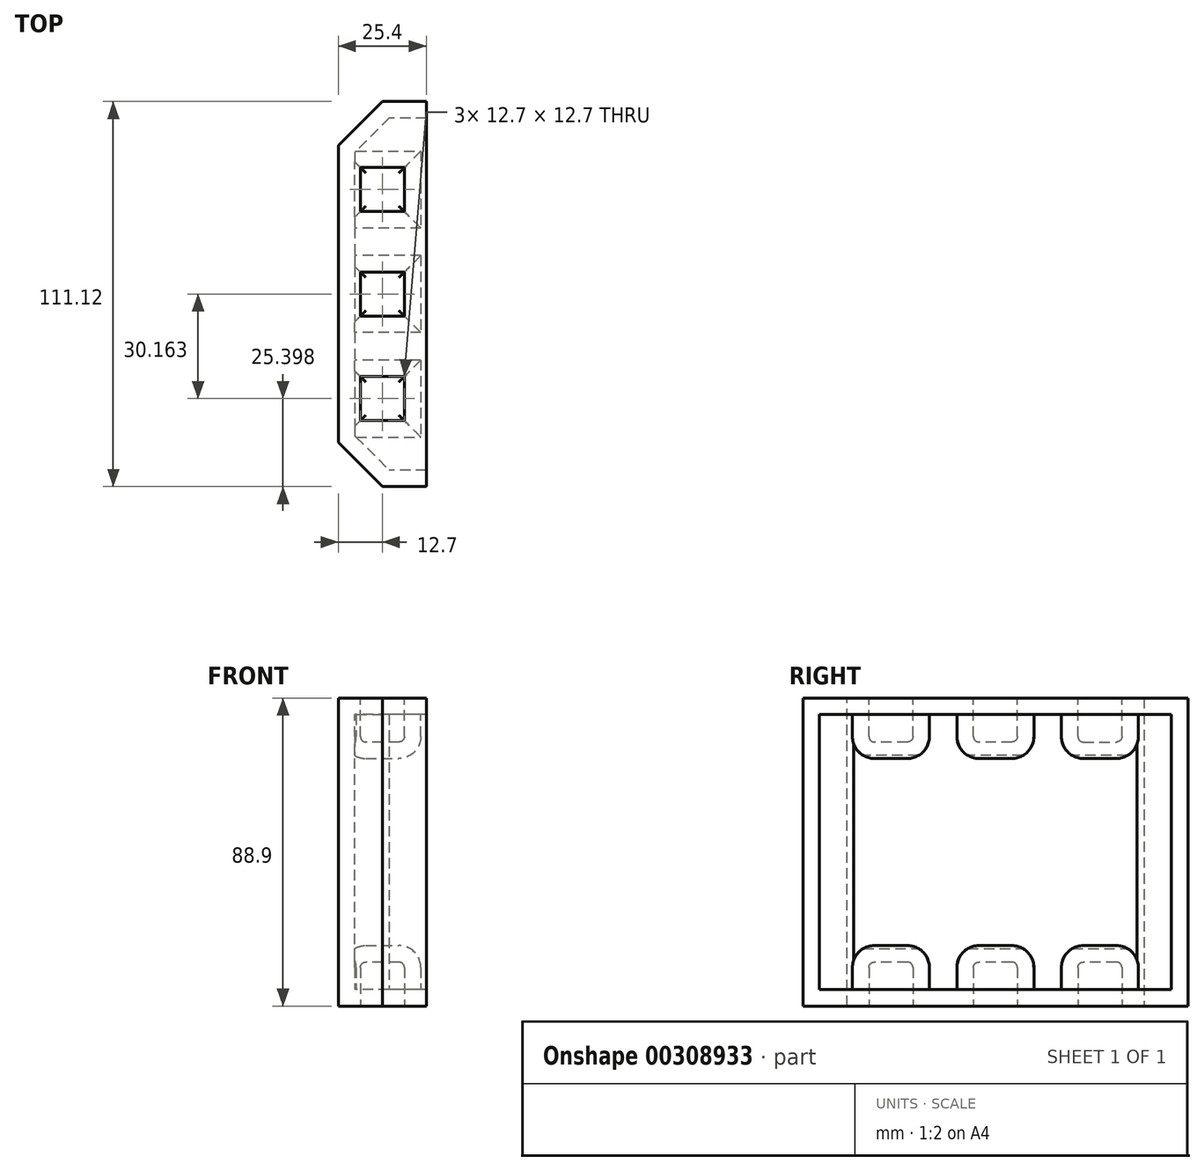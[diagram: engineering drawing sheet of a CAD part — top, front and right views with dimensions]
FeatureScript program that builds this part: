
annotation { "Feature Type Name" : "Feature", "Feature Type Description" : "" }
export const myFeature = defineFeature(function(context is Context, id is Id, definition is map)
    precondition{}
    {
        {
            var Q0;
            Q0=qCreatedBy(makeId("Right.planeOp"),FACE);
            var sketch = newSketch(context, id + "F0", { "sketchPlane" : qUnion([Q0])});
            skLineSegment(sketch, "E0.bottom", {"start": v(55.56, -44.45) * mm, "end": v(-55.56, -44.45) * mm});
            skLineSegment(sketch, "E0.top", {"start": v(55.56, 44.45) * mm, "end": v(-55.56, 44.45) * mm});
            skLineSegment(sketch, "E0.left", {"start": v(55.56, -44.45) * mm, "end": v(55.56, 44.45) * mm});
            skLineSegment(sketch, "E0.right", {"start": v(-55.56, -44.45) * mm, "end": v(-55.56, 44.45) * mm});
            skPoint(sketch, "E0.middle", {"position": v(0, 0) * mm});
            skSolve(sketch);
        }
        {
            var Q0;
            Q0=qSketchRegion(id+"F0",true);
            extrude(context, id + "F1", {"entities" : qUnion([Q0]), "depth" : 25.4 * mm});
        }
        {
            var Q0;
            Q0=makeQuery(id+"F1.opExtrude","CAP_EDGE",EDGE,{"disambiguationData":[OSD([sQuery(id+"F0.wireOp",EDGE,"E0.right")])],"isStart":true});
            var Q1;
            Q1=makeQuery(id+"F1.opExtrude","CAP_EDGE",EDGE,{"disambiguationData":[OSD([sQuery(id+"F0.wireOp",EDGE,"E0.left")])],"isStart":true});
            chamfer(context, id + "F2", {"entities" : qUnion([Q0, Q1]), "width" : 12.7 * mm, "tangentPropagation" : true});
        }
        {
            var Q0;
            Q0=makeQuery(id+"F1.opExtrude","SWEPT_FACE",FACE,{"disambiguationData":[OSD([sQuery(id+"F0.wireOp",EDGE,"E0.top")])]});
            var sketch = newSketch(context, id + "F3", { "sketchPlane" : qUnion([Q0])});
            skLineSegment(sketch, "E1.bottom", {"start": v(19.05, 23.81) * mm, "end": v(6.35, 23.81) * mm});
            skLineSegment(sketch, "E1.top", {"start": v(19.05, 36.51) * mm, "end": v(6.35, 36.51) * mm});
            skLineSegment(sketch, "E1.left", {"start": v(19.05, 23.81) * mm, "end": v(19.05, 36.51) * mm});
            skLineSegment(sketch, "E1.right", {"start": v(6.35, 23.81) * mm, "end": v(6.35, 36.51) * mm});
            skPoint(sketch, "E1.middle", {"position": v(12.7, 30.16) * mm});
            skPoint(sketch, "E1.cornerSnap0", {"position": v(19.05, 55.56) * mm});
            skLineSegment(sketch, "E2.bottom", {"start": v(19.05, -23.81) * mm, "end": v(6.35, -23.81) * mm});
            skLineSegment(sketch, "E2.top", {"start": v(19.05, -36.51) * mm, "end": v(6.35, -36.51) * mm});
            skLineSegment(sketch, "E2.left", {"start": v(19.05, -23.81) * mm, "end": v(19.05, -36.51) * mm});
            skLineSegment(sketch, "E2.right", {"start": v(6.35, -23.81) * mm, "end": v(6.35, -36.51) * mm});
            skPoint(sketch, "E2.middle", {"position": v(12.7, -30.16) * mm});
            skPoint(sketch, "E2.cornerSnap0", {"position": v(19.05, -55.56) * mm});
            skLineSegment(sketch, "E3.bottom", {"start": v(19.05, 6.35) * mm, "end": v(6.35, 6.35) * mm});
            skLineSegment(sketch, "E3.top", {"start": v(19.05, -6.35) * mm, "end": v(6.35, -6.35) * mm});
            skLineSegment(sketch, "E3.left", {"start": v(19.05, 6.35) * mm, "end": v(19.05, -6.35) * mm});
            skLineSegment(sketch, "E3.right", {"start": v(6.35, 6.35) * mm, "end": v(6.35, -6.35) * mm});
            skPoint(sketch, "E3.middle", {"position": v(12.7, 0) * mm});
            skSolve(sketch);
        }
        {
            var Q0;
            Q0=qSketchRegion(id+"F3",true);
            extrude(context, id + "F4", {"entities" : qUnion([Q0]), "operationType" : NewBodyOperationType.REMOVE, "oppositeDirection" : true, "depth" : 12.7 * mm});
        }
        {
            var Q0;
            Q0=makeQuery(id+"F4.boolean.opBoolean","COPY",FACE,{"derivedFrom":makeQuery(id+"F4.opExtrude","CAP_FACE",FACE,{"disambiguationData":[OSD([sQuery(id+"F3.wireOp",EDGE,"E1.bottom"),sQuery(id+"F3.wireOp",EDGE,"E1.top"),sQuery(id+"F3.wireOp",EDGE,"E1.left"),sQuery(id+"F3.wireOp",EDGE,"E1.right")])],"isStart":false})});
            var Q1;
            Q1=makeQuery(id+"F4.boolean.opBoolean","COPY",FACE,{"derivedFrom":makeQuery(id+"F4.opExtrude","CAP_FACE",FACE,{"disambiguationData":[OSD([sQuery(id+"F3.wireOp",EDGE,"E3.bottom"),sQuery(id+"F3.wireOp",EDGE,"E3.top"),sQuery(id+"F3.wireOp",EDGE,"E3.left"),sQuery(id+"F3.wireOp",EDGE,"E3.right")])],"isStart":false})});
            var Q2;
            Q2=makeQuery(id+"F4.boolean.opBoolean","COPY",FACE,{"derivedFrom":makeQuery(id+"F4.opExtrude","CAP_FACE",FACE,{"disambiguationData":[OSD([sQuery(id+"F3.wireOp",EDGE,"E2.bottom"),sQuery(id+"F3.wireOp",EDGE,"E2.top"),sQuery(id+"F3.wireOp",EDGE,"E2.left"),sQuery(id+"F3.wireOp",EDGE,"E2.right")])],"isStart":false})});
            fillet(context, id + "F5", {"entities" : qUnion([Q0, Q1, Q2]), "radius" : 1.59 * mm, "tangentPropagation" : true, "allowEdgeOverflow" : false});
        }
        {
            var Q0;
            Q0=makeQuery(id+"F1.opExtrude","SWEPT_FACE",FACE,{"disambiguationData":[OSD([sQuery(id+"F0.wireOp",EDGE,"E0.bottom")])]});
            var sketch = newSketch(context, id + "F6", { "sketchPlane" : qUnion([Q0])});
            skLineSegment(sketch, "E4.bottom", {"start": v(19.05, 23.81) * mm, "end": v(6.35, 23.81) * mm});
            skLineSegment(sketch, "E4.top", {"start": v(19.05, 36.51) * mm, "end": v(6.35, 36.51) * mm});
            skLineSegment(sketch, "E4.left", {"start": v(19.05, 23.81) * mm, "end": v(19.05, 36.51) * mm});
            skLineSegment(sketch, "E4.right", {"start": v(6.35, 23.81) * mm, "end": v(6.35, 36.51) * mm});
            skPoint(sketch, "E4.middle", {"position": v(12.7, 30.16) * mm});
            skPoint(sketch, "E4.cornerSnap0", {"position": v(19.05, 55.56) * mm});
            skLineSegment(sketch, "E5.bottom", {"start": v(19.05, -36.51) * mm, "end": v(6.35, -36.51) * mm});
            skLineSegment(sketch, "E5.top", {"start": v(19.05, -23.81) * mm, "end": v(6.35, -23.81) * mm});
            skLineSegment(sketch, "E5.left", {"start": v(19.05, -36.51) * mm, "end": v(19.05, -23.81) * mm});
            skLineSegment(sketch, "E5.right", {"start": v(6.35, -36.51) * mm, "end": v(6.35, -23.81) * mm});
            skPoint(sketch, "E5.middle", {"position": v(12.7, -30.16) * mm});
            skPoint(sketch, "E5.cornerSnap0", {"position": v(19.05, -55.56) * mm});
            skLineSegment(sketch, "E6.bottom", {"start": v(19.05, -6.35) * mm, "end": v(6.35, -6.35) * mm});
            skLineSegment(sketch, "E6.top", {"start": v(19.05, 6.35) * mm, "end": v(6.35, 6.35) * mm});
            skLineSegment(sketch, "E6.left", {"start": v(19.05, -6.35) * mm, "end": v(19.05, 6.35) * mm});
            skLineSegment(sketch, "E6.right", {"start": v(6.35, -6.35) * mm, "end": v(6.35, 6.35) * mm});
            skPoint(sketch, "E6.middle", {"position": v(12.7, 0) * mm});
            skPoint(sketch, "E6.middle.positionSnap0", {"position": v(12.7, 23.81) * mm});
            skPoint(sketch, "E6.middle.positionSnap1", {"position": v(25.4, 0) * mm});
            skPoint(sketch, "E6.centerSnap0", {"position": v(12.7, 23.81) * mm});
            skPoint(sketch, "E6.centerSnap1", {"position": v(25.4, 0) * mm});
            skSolve(sketch);
        }
        {
            var Q0;
            Q0=qSketchRegion(id+"F6",true);
            extrude(context, id + "F7", {"entities" : qUnion([Q0]), "operationType" : NewBodyOperationType.REMOVE, "oppositeDirection" : true, "depth" : 12.7 * mm});
        }
        {
            var Q0;
            Q0=makeQuery(id+"F7.boolean.opBoolean","COPY",FACE,{"derivedFrom":makeQuery(id+"F7.opExtrude","CAP_FACE",FACE,{"disambiguationData":[OSD([sQuery(id+"F6.wireOp",EDGE,"E4.bottom"),sQuery(id+"F6.wireOp",EDGE,"E4.top"),sQuery(id+"F6.wireOp",EDGE,"E4.left"),sQuery(id+"F6.wireOp",EDGE,"E4.right")])],"isStart":false})});
            var Q1;
            Q1=makeQuery(id+"F7.boolean.opBoolean","COPY",FACE,{"derivedFrom":makeQuery(id+"F7.opExtrude","CAP_FACE",FACE,{"disambiguationData":[OSD([sQuery(id+"F6.wireOp",EDGE,"E6.bottom"),sQuery(id+"F6.wireOp",EDGE,"E6.top"),sQuery(id+"F6.wireOp",EDGE,"E6.left"),sQuery(id+"F6.wireOp",EDGE,"E6.right")])],"isStart":false})});
            var Q2;
            Q2=makeQuery(id+"F7.boolean.opBoolean","COPY",FACE,{"derivedFrom":makeQuery(id+"F7.opExtrude","CAP_FACE",FACE,{"disambiguationData":[OSD([sQuery(id+"F6.wireOp",EDGE,"E5.bottom"),sQuery(id+"F6.wireOp",EDGE,"E5.top"),sQuery(id+"F6.wireOp",EDGE,"E5.left"),sQuery(id+"F6.wireOp",EDGE,"E5.right")])],"isStart":false})});
            fillet(context, id + "F8", {"entities" : qUnion([Q0, Q1, Q2]), "radius" : 1.59 * mm, "tangentPropagation" : true, "allowEdgeOverflow" : false});
        }
        {
            var Q0;
            Q0=makeQuery(id+"F1.opExtrude","CAP_FACE",FACE,{"disambiguationData":[OSD([sQuery(id+"F0.wireOp",EDGE,"E0.bottom"),sQuery(id+"F0.wireOp",EDGE,"E0.top"),sQuery(id+"F0.wireOp",EDGE,"E0.left"),sQuery(id+"F0.wireOp",EDGE,"E0.right")])],"isStart":false});
            shell(context, id + "F9", {"entities" : qUnion([Q0]), "thickness" : 4.76 * mm});
        }
    });
